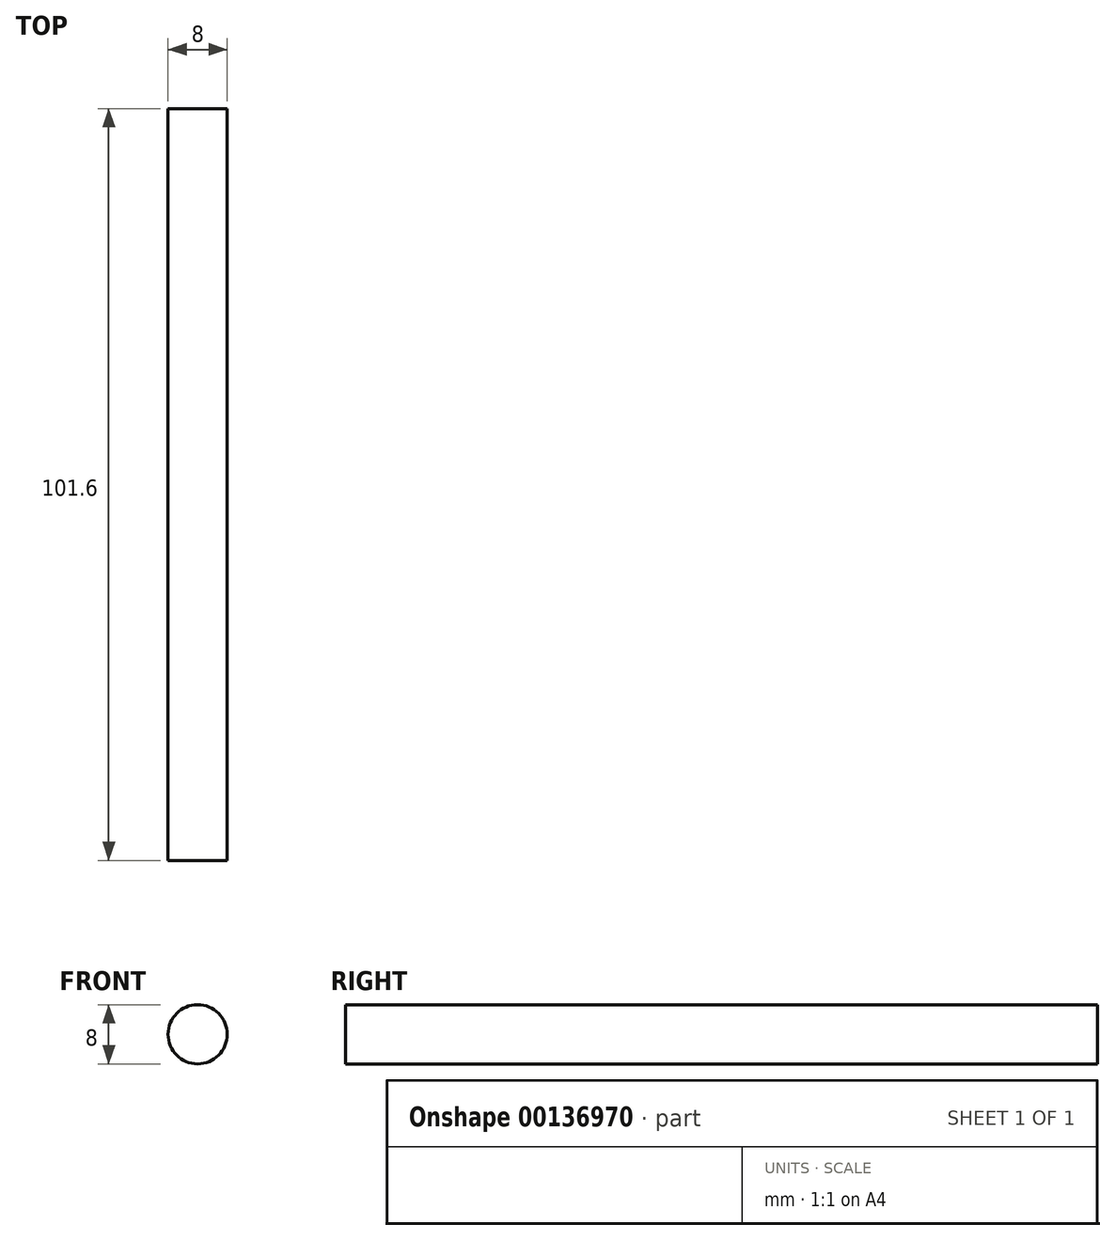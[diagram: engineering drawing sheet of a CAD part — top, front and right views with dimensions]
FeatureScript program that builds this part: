
annotation { "Feature Type Name" : "Feature", "Feature Type Description" : "" }
export const myFeature = defineFeature(function(context is Context, id is Id, definition is map)
    precondition{}
    {
        {
            var Q0;
            Q0=qCreatedBy(makeId("Front.planeOp"),FACE);
            var sketch = newSketch(context, id + "F0", { "sketchPlane" : qUnion([Q0])});
            skCircle(sketch, "E0", {"center": v(1.52, 0) * mm, "radius": 4 * mm});
            skSolve(sketch);
        }
        {
            var Q0;
            Q0=makeQuery(id+"F0.imprint","IMPRINT",FACE,{"disambiguationData":[TD([[makeQuery(id+"F0.imprint","IMPRINT",EDGE,{"derivedFrom":sQuery(id+"F0.wireOp",EDGE,"E0")}),1.0]])]});
            extrude(context, id + "F1", {"entities" : qUnion([Q0]), "depth" : 101.6 * mm});
        }
    });
